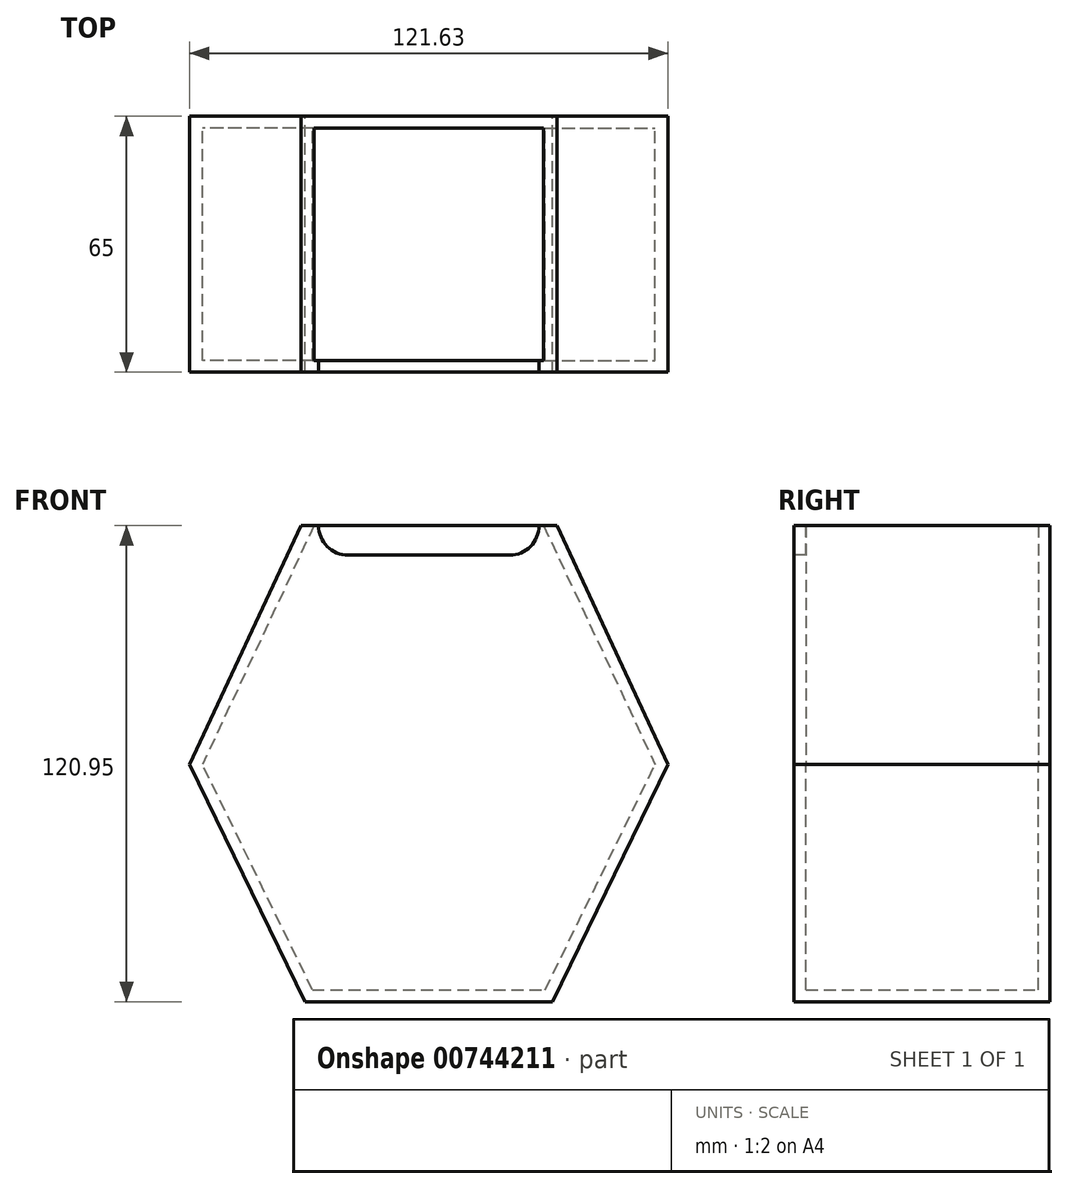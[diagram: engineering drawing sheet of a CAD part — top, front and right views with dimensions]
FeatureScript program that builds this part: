
annotation { "Feature Type Name" : "Feature", "Feature Type Description" : "" }
export const myFeature = defineFeature(function(context is Context, id is Id, definition is map)
    precondition{}
    {
        {
            var Q0;
            Q0=qCreatedBy(makeId("Front.planeOp"),FACE);
            var sketch = newSketch(context, id + "F0", { "sketchPlane" : qUnion([Q0])});
            skLineSegment(sketch, "E0", {"start": v(-51.37, 74.96) * mm, "end": v(-79.69, 14.23) * mm});
            skLineSegment(sketch, "E1", {"start": v(13.63, 74.96) * mm, "end": v(41.94, 14.23) * mm});
            skLineSegment(sketch, "E2", {"start": v(-50.32, -45.99) * mm, "end": v(-79.69, 14.23) * mm});
            skLineSegment(sketch, "E3", {"start": v(12.57, -45.99) * mm, "end": v(41.94, 14.23) * mm});
            skLineSegment(sketch, "E4", {"start": v(-50.32, -45.99) * mm, "end": v(12.57, -45.99) * mm});
            skLineSegment(sketch, "E5", {"start": v(-51.37, 74.96) * mm, "end": v(13.63, 74.96) * mm});
            skSolve(sketch);
        }
        {
            var Q0;
            Q0=makeQuery(id+"F0.imprint","IMPRINT",FACE,{"disambiguationData":[TD([[makeQuery(id+"F0.imprint","IMPRINT",EDGE,{"derivedFrom":sQuery(id+"F0.wireOp",EDGE,"E0")}),1.0]])]});
            extrude(context, id + "F1", {"entities" : qUnion([Q0]), "depth" : 65 * mm, "offsetDistance" : 25 * mm});
        }
        {
            var Q0;
            Q0=makeQuery(id+"F1.opExtrude","SWEPT_FACE",FACE,{"disambiguationData":[OSD([sQuery(id+"F0.wireOp",EDGE,"E5")])]});
            shell(context, id + "F2", {"entities" : qUnion([Q0]), "thickness" : 3 * mm});
        }
        {
            var Q0;
            Q0=makeQuery(id+"F1.opExtrude","CAP_FACE",FACE,{"disambiguationData":[OSD([sQuery(id+"F0.wireOp",EDGE,"E0"),sQuery(id+"F0.wireOp",EDGE,"E1"),sQuery(id+"F0.wireOp",EDGE,"E2"),sQuery(id+"F0.wireOp",EDGE,"E3"),sQuery(id+"F0.wireOp",EDGE,"E4"),sQuery(id+"F0.wireOp",EDGE,"E5")])],"isStart":false});
            var sketch = newSketch(context, id + "F3", { "sketchPlane" : qUnion([Q0])});
            skLineSegment(sketch, "E6", {"start": v(-39.37, 67.46) * mm, "end": v(1.63, 67.46) * mm});
            skPoint(sketch, "E7.center.orphan", {"position": v(1.63, 74.96) * mm});
            skArc(sketch, "E8", {"start": v(1.63, 67.46) * mm, "mid": v(6.93, 69.65) * mm, "end": v(9.13, 74.96) * mm});
            skPoint(sketch, "E9.center.orphan", {"position": v(-39.37, 74.96) * mm});
            skArc(sketch, "E10", {"start": v(-39.37, 67.46) * mm, "mid": v(-44.68, 69.65) * mm, "end": v(-46.87, 74.96) * mm});
            skLineSegment(sketch, "E11", {"start": v(-46.87, 74.96) * mm, "end": v(9.13, 74.96) * mm});
            skSolve(sketch);
        }
        {
            var Q0;
            Q0=makeQuery(id+"F3.imprint","IMPRINT",FACE,{"disambiguationData":[TD([[makeQuery(id+"F3.imprint","IMPRINT",EDGE,{"derivedFrom":sQuery(id+"F3.wireOp",EDGE,"E6")}),1.0]])]});
            extrude(context, id + "F4", {"entities" : qUnion([Q0]), "operationType" : NewBodyOperationType.REMOVE, "oppositeDirection" : true, "depth" : 25 * mm, "offsetDistance" : 25 * mm});
        }
    });
